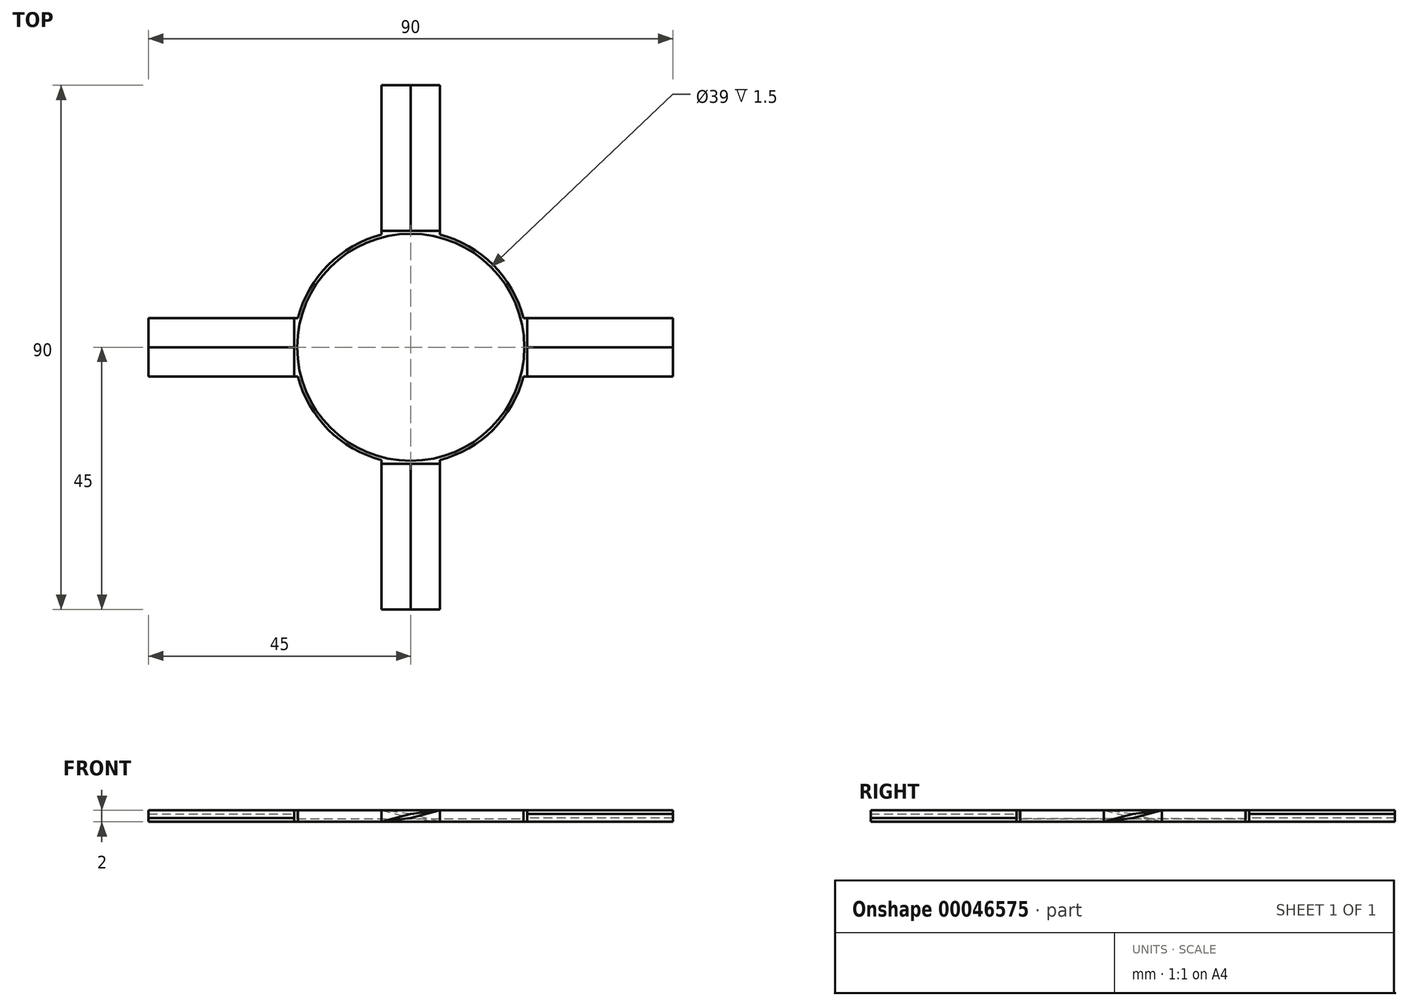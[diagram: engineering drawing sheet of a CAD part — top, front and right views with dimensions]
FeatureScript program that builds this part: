
annotation { "Feature Type Name" : "Feature", "Feature Type Description" : "" }
export const myFeature = defineFeature(function(context is Context, id is Id, definition is map)
    precondition{}
    {
        {
            var Q0;
            Q0=qCreatedBy(makeId("Front.planeOp"),FACE);
            var sketch = newSketch(context, id + "F0", { "sketchPlane" : qUnion([Q0])});
            skLineSegment(sketch, "E0.bottom", {"start": v(-20, 2) * mm, "end": v(0, 2) * mm});
            skLineSegment(sketch, "E0.top", {"start": v(-20, 0) * mm, "end": v(0, 0) * mm});
            skLineSegment(sketch, "E0.left", {"start": v(-20, 2) * mm, "end": v(-20, 0) * mm});
            skLineSegment(sketch, "E0.right", {"start": v(0, 2) * mm, "end": v(0, 0) * mm});
            skSolve(sketch);
        }
        {
            var Q0;
            Q0 = qSketchRegion(id + "F0", true);
            var Q1;
            Q1=sQuery(id+"F0.wireOp",EDGE,"E0.left");
            var Q2;
            Q2=sQuery(id+"F0.wireOp",EDGE,"E0.top");
            var Q3;
            Q3=sQuery(id+"F0.wireOp",EDGE,"E0.bottom");
            var Q4;
            Q4=sQuery(id+"F0.wireOp",EDGE,"E0.right");
            revolve(context, id + "F1", {"entities" : qUnion([Q0]), "surfaceEntities" : qUnion([Q1, Q2, Q3]), "axis" : qUnion([Q4]), "revolveType" : RevolveType.FULL});
        }
        {
            var Q0;
            Q0=makeQuery(id+"F1.opRevolve","SWEPT_FACE",FACE,{"disambiguationData":[OSD([sQuery(id+"F0.wireOp",EDGE,"E0.bottom")])]});
            shell(context, id + "F2", {"entities" : qUnion([Q0]), "thickness" : 0.5 * mm});
        }
        {
            var Q0;
            Q0=qCreatedBy(makeId("Top.planeOp"),FACE);
            var sketch = newSketch(context, id + "F3", { "sketchPlane" : qUnion([Q0])});
            skLineSegment(sketch, "E1.bottom", {"start": v(-5, 20) * mm, "end": v(0, 20) * mm});
            skLineSegment(sketch, "E1.left", {"start": v(-5, 20) * mm, "end": v(-5, 19.36) * mm});
            skLineSegment(sketch, "E1.right", {"start": v(0, 20) * mm, "end": v(0, 0) * mm});
            skLineSegment(sketch, "E2.MirrorCS", {"start": v(5, 20) * mm, "end": v(0, 20) * mm});
            skLineSegment(sketch, "E3.MirrorCS", {"start": v(5, 20) * mm, "end": v(5, 19.36) * mm});
            skLineSegment(sketch, "E4.MirrorCS", {"start": v(-5, -20) * mm, "end": v(-5, -19.36) * mm});
            skLineSegment(sketch, "E5.MirrorCS", {"start": v(0, -20) * mm, "end": v(0, 0) * mm});
            skLineSegment(sketch, "E6.MirrorCS", {"start": v(5, -20) * mm, "end": v(5, -19.36) * mm});
            skLineSegment(sketch, "E7.MirrorCS", {"start": v(-5, -20) * mm, "end": v(0, -20) * mm});
            skLineSegment(sketch, "E8.MirrorCS", {"start": v(5, -20) * mm, "end": v(0, -20) * mm});
            skArc(sketch, "E9", {"start": v(-5, -19.36) * mm, "mid": v(0, -20) * mm, "end": v(5, -19.36) * mm});
            skPoint(sketch, "E10.MirrorCS.start.orphan", {"position": v(-5, 0) * mm});
            skPoint(sketch, "E11.MirrorCS.start.orphan", {"position": v(5, 0) * mm});
            skArc(sketch, "E12.trimOffspring", {"start": v(5, 19.36) * mm, "mid": v(0, 20) * mm, "end": v(-5, 19.36) * mm});
            skLineSegment(sketch, "E13.bottom", {"start": v(20, 0) * mm, "end": v(0, 0) * mm});
            skLineSegment(sketch, "E13.top", {"start": v(20, 5) * mm, "end": v(19.36, 5) * mm});
            skLineSegment(sketch, "E13.left", {"start": v(20, 0) * mm, "end": v(20, 5) * mm});
            skLineSegment(sketch, "E13.right", {"start": v(0, 0) * mm, "end": v(0, 5) * mm});
            skLineSegment(sketch, "E14.MirrorCS", {"start": v(20, -5) * mm, "end": v(19.36, -5) * mm});
            skLineSegment(sketch, "E15.MirrorCS", {"start": v(20, 0) * mm, "end": v(20, -5) * mm});
            skLineSegment(sketch, "E16.MirrorCS", {"start": v(-5, 0) * mm, "end": v(0, 0) * mm});
            skLineSegment(sketch, "E17.MirrorCS", {"start": v(-20, -5) * mm, "end": v(-19.36, -5) * mm});
            skLineSegment(sketch, "E18.MirrorCS", {"start": v(-20, 0) * mm, "end": v(0, 0) * mm});
            skLineSegment(sketch, "E19.MirrorCS", {"start": v(-20, 0) * mm, "end": v(-20, 5) * mm});
            skLineSegment(sketch, "E20.MirrorCS", {"start": v(-20, 0) * mm, "end": v(-20, -5) * mm});
            skLineSegment(sketch, "E21.MirrorCS", {"start": v(-20, 5) * mm, "end": v(-19.36, 5) * mm});
            skArc(sketch, "E22", {"start": v(-19.36, 5) * mm, "mid": v(-20, 0) * mm, "end": v(-19.36, -5) * mm});
            skArc(sketch, "E23.trimOffspring", {"start": v(19.36, -5) * mm, "mid": v(20, 0) * mm, "end": v(19.36, 5) * mm});
            skPoint(sketch, "E24.orphan", {"position": v(0, 5) * mm});
            skPoint(sketch, "E25.orphan", {"position": v(0, -5) * mm});
            skSolve(sketch);
        }
        {
            var Q0;
            Q0 = qSketchRegion(id + "F3", true);
            extrude(context, id + "F4", {"entities" : qUnion([Q0]), "operationType" : NewBodyOperationType.ADD, "depth" : 2 * mm});
        }
        {
            var Q0;
            Q0=makeQuery(id+"F4.boolean.opBoolean","MERGE",FACE,{"derivedFrom":[makeQuery(id+"F4.opExtrude","SWEPT_FACE",FACE,{"disambiguationData":[OSD([sQuery(id+"F3.wireOp",EDGE,"E7.MirrorCS")])]}),makeQuery(id+"F4.opExtrude","SWEPT_FACE",FACE,{"disambiguationData":[OSD([sQuery(id+"F3.wireOp",EDGE,"E8.MirrorCS")])]})]});
            var sketch = newSketch(context, id + "F5", { "sketchPlane" : qUnion([Q0])});
            skLineSegment(sketch, "E26", {"start": v(-5, 0) * mm, "end": v(0, 1.33) * mm});
            skLineSegment(sketch, "E27", {"start": v(-5, 0) * mm, "end": v(0, 0.67) * mm});
            skLineSegment(sketch, "E28", {"start": v(0, 1.33) * mm, "end": v(0, 2) * mm, "construction": true});
            skLineSegment(sketch, "E29", {"start": v(0, 1.33) * mm, "end": v(0, 0.67) * mm, "construction": true});
            skLineSegment(sketch, "E30", {"start": v(0, 0.67) * mm, "end": v(0, 0) * mm, "construction": true});
            skLineSegment(sketch, "E31", {"start": v(0, 1.33) * mm, "end": v(5, 2) * mm});
            skLineSegment(sketch, "E32", {"start": v(0, 0.67) * mm, "end": v(5, 2) * mm});
            skSolve(sketch);
        }
        {
            var Q0;
            Q0 = qSketchRegion(id + "F5", true);
            extrude(context, id + "F6", {"entities" : qUnion([Q0]), "operationType" : NewBodyOperationType.ADD, "depth" : 25 * mm});
        }
        {
            var Q0;
            Q0=makeQuery(id+"F4.boolean.opBoolean","MERGE",FACE,{"derivedFrom":[makeQuery(id+"F4.opExtrude","SWEPT_FACE",FACE,{"disambiguationData":[OSD([sQuery(id+"F3.wireOp",EDGE,"E1.bottom")])]}),makeQuery(id+"F4.opExtrude","SWEPT_FACE",FACE,{"disambiguationData":[OSD([sQuery(id+"F3.wireOp",EDGE,"E2.MirrorCS")])]})]});
            var sketch = newSketch(context, id + "F7", { "sketchPlane" : qUnion([Q0])});
            skLineSegment(sketch, "E33", {"start": v(5, 2) * mm, "end": v(0, 0.67) * mm});
            skLineSegment(sketch, "E34", {"start": v(0, 1.33) * mm, "end": v(5, 2) * mm});
            skLineSegment(sketch, "E35", {"start": v(0, 0) * mm, "end": v(0, 0.67) * mm, "construction": true});
            skLineSegment(sketch, "E36", {"start": v(0, 2) * mm, "end": v(0, 1.33) * mm, "construction": true});
            skLineSegment(sketch, "E37", {"start": v(0, 1.33) * mm, "end": v(0, 0.67) * mm, "construction": true});
            skLineSegment(sketch, "E38", {"start": v(0, 0.67) * mm, "end": v(-5, 0) * mm});
            skLineSegment(sketch, "E39", {"start": v(-5, 0) * mm, "end": v(0, 1.33) * mm});
            skSolve(sketch);
        }
        {
            var Q0;
            Q0 = qSketchRegion(id + "F7", true);
            extrude(context, id + "F8", {"entities" : qUnion([Q0]), "operationType" : NewBodyOperationType.ADD, "depth" : 25 * mm});
        }
        {
            var Q0;
            Q0=makeQuery(id+"F4.boolean.opBoolean","MERGE",FACE,{"derivedFrom":[makeQuery(id+"F4.opExtrude","SWEPT_FACE",FACE,{"disambiguationData":[OSD([sQuery(id+"F3.wireOp",EDGE,"E13.left")])]}),makeQuery(id+"F4.opExtrude","SWEPT_FACE",FACE,{"disambiguationData":[OSD([sQuery(id+"F3.wireOp",EDGE,"E15.MirrorCS")])]})]});
            var sketch = newSketch(context, id + "F9", { "sketchPlane" : qUnion([Q0])});
            skLineSegment(sketch, "E40", {"start": v(-5, 0) * mm, "end": v(0, 1.33) * mm});
            skLineSegment(sketch, "E41", {"start": v(0, 1.33) * mm, "end": v(0, 0.67) * mm});
            skLineSegment(sketch, "E42", {"start": v(0, 0.67) * mm, "end": v(-5, 0) * mm});
            skLineSegment(sketch, "E43", {"start": v(5, 2) * mm, "end": v(0, 1.33) * mm});
            skLineSegment(sketch, "E44", {"start": v(5, 2) * mm, "end": v(0, 0.67) * mm});
            skLineSegment(sketch, "E45", {"start": v(0, 1.33) * mm, "end": v(0, 2) * mm});
            skLineSegment(sketch, "E46", {"start": v(0, 0.67) * mm, "end": v(0, 0) * mm});
            skSolve(sketch);
        }
        {
            var Q0;
            Q0 = qSketchRegion(id + "F9", true);
            extrude(context, id + "F10", {"entities" : qUnion([Q0]), "operationType" : NewBodyOperationType.ADD, "depth" : 25 * mm});
        }
        {
            var Q0;
            Q0=makeQuery(id+"F4.boolean.opBoolean","MERGE",FACE,{"derivedFrom":[makeQuery(id+"F4.opExtrude","SWEPT_FACE",FACE,{"disambiguationData":[OSD([sQuery(id+"F3.wireOp",EDGE,"E19.MirrorCS")])]}),makeQuery(id+"F4.opExtrude","SWEPT_FACE",FACE,{"disambiguationData":[OSD([sQuery(id+"F3.wireOp",EDGE,"E20.MirrorCS")])]})]});
            var sketch = newSketch(context, id + "F11", { "sketchPlane" : qUnion([Q0])});
            skLineSegment(sketch, "E47", {"start": v(-5, 0) * mm, "end": v(0, 1.33) * mm});
            skLineSegment(sketch, "E48", {"start": v(0, 1.33) * mm, "end": v(5, 2) * mm});
            skLineSegment(sketch, "E49", {"start": v(5, 2) * mm, "end": v(0, 0.67) * mm});
            skLineSegment(sketch, "E50", {"start": v(0, 0.67) * mm, "end": v(-5, 0) * mm});
            skLineSegment(sketch, "E51", {"start": v(0, 2) * mm, "end": v(0, 1.33) * mm});
            skLineSegment(sketch, "E52", {"start": v(0, 1.33) * mm, "end": v(0, 0.67) * mm});
            skLineSegment(sketch, "E53", {"start": v(0, 0.67) * mm, "end": v(0, 0) * mm});
            skSolve(sketch);
        }
        {
            var Q0;
            Q0 = qSketchRegion(id + "F11", true);
            extrude(context, id + "F12", {"entities" : qUnion([Q0]), "operationType" : NewBodyOperationType.ADD, "depth" : 25 * mm});
        }
    });
